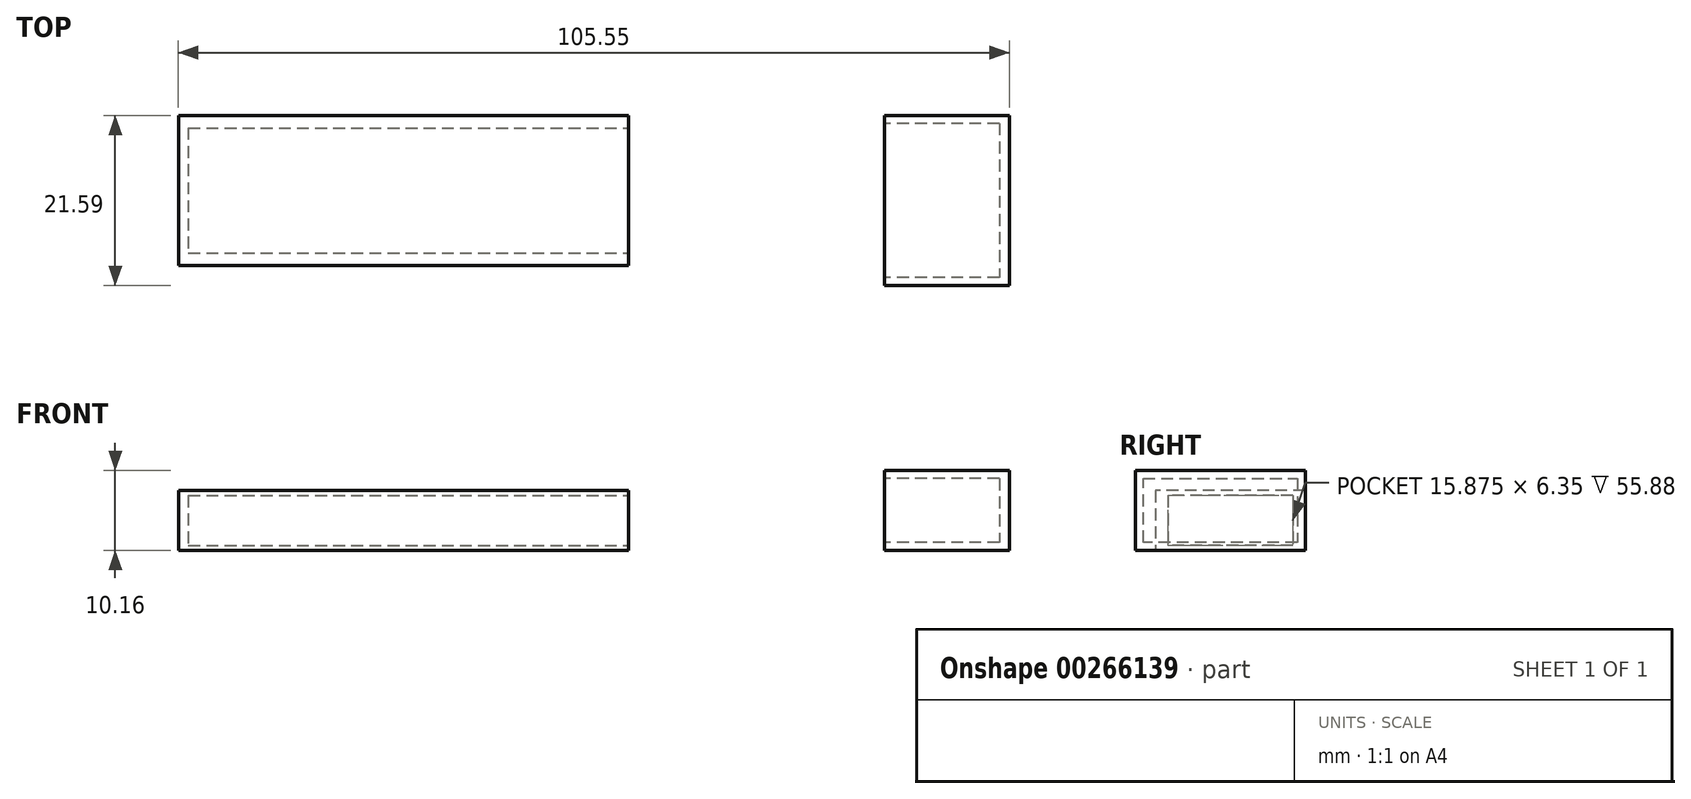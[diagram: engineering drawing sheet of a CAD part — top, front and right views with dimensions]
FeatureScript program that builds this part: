
annotation { "Feature Type Name" : "Feature", "Feature Type Description" : "" }
export const myFeature = defineFeature(function(context is Context, id is Id, definition is map)
    precondition{}
    {
        {
            var Q0;
            Q0=qCreatedBy(makeId("Top.planeOp"),FACE);
            var sketch = newSketch(context, id + "F0", { "sketchPlane" : qUnion([Q0])});
            skLineSegment(sketch, "E0.bottom", {"start": v(-57.67, 16.7) * mm, "end": v(-0.52, 16.7) * mm});
            skLineSegment(sketch, "E0.top", {"start": v(-57.67, -2.35) * mm, "end": v(-0.52, -2.35) * mm});
            skLineSegment(sketch, "E0.left", {"start": v(-57.67, 16.7) * mm, "end": v(-57.67, -2.35) * mm});
            skLineSegment(sketch, "E0.right", {"start": v(-0.52, 16.7) * mm, "end": v(-0.52, -2.35) * mm});
            skLineSegment(sketch, "E1.bottom", {"start": v(32, 16.7) * mm, "end": v(47.88, 16.7) * mm});
            skLineSegment(sketch, "E1.top", {"start": v(32, -4.9) * mm, "end": v(47.88, -4.9) * mm});
            skLineSegment(sketch, "E1.left", {"start": v(32, 16.7) * mm, "end": v(32, -4.9) * mm});
            skLineSegment(sketch, "E1.right", {"start": v(47.88, 16.7) * mm, "end": v(47.88, -4.9) * mm});
            skFitSpline(sketch, "E2", {"points": [v(-57.67, 7.17) * mm, v(-71.95, 19.43) * mm, v(-49.66, 49.56) * mm, v(30.53, 57.4) * mm, v(72.3, 17.31) * mm, v(47.88, 5.9) * mm], "startDerivative": vector(-182.05, 0) * mm, "endDerivative": vector(-254.37, 0) * mm});
            skSolve(sketch);
        }
        {
            var Q0;
            Q0=makeQuery(id+"F0.imprint","IMPRINT",FACE,{"disambiguationData":[TD([[makeQuery(id+"F0.imprint","IMPRINT",EDGE,{"derivedFrom":sQuery(id+"F0.wireOp",EDGE,"E0.bottom")}),-1.0]])]});
            extrude(context, id + "F1", {"entities" : qUnion([Q0]), "depth" : 7.62 * mm});
        }
        {
            var Q0;
            Q0=makeQuery(id+"F0.imprint","IMPRINT",FACE,{"disambiguationData":[TD([[makeQuery(id+"F0.imprint","IMPRINT",EDGE,{"derivedFrom":sQuery(id+"F0.wireOp",EDGE,"E1.bottom")}),-1.0]])]});
            extrude(context, id + "F2", {"entities" : qUnion([Q0]), "depth" : 10.16 * mm});
        }
        {
            var Q0;
            Q0=makeQuery(id+"F1.opExtrude","SWEPT_FACE",FACE,{"disambiguationData":[OSD([sQuery(id+"F0.wireOp",EDGE,"E0.right")])]});
            var sketch = newSketch(context, id + "F3", { "sketchPlane" : qUnion([Q0])});
            skLineSegment(sketch, "E3.0", {"start": v(15.11, 6.99) * mm, "end": v(-0.76, 6.99) * mm});
            skLineSegment(sketch, "E3.1", {"start": v(15.11, 6.99) * mm, "end": v(15.11, 0.64) * mm});
            skLineSegment(sketch, "E3.3", {"start": v(-0.76, 6.99) * mm, "end": v(-0.76, 0.63) * mm});
            skLineSegment(sketch, "E4", {"start": v(15.11, 0.63) * mm, "end": v(-0.76, 0.63) * mm});
            skSolve(sketch);
        }
        {
            var Q0;
            Q0=makeQuery(id+"F2.opExtrude","SWEPT_FACE",FACE,{"disambiguationData":[OSD([sQuery(id+"F0.wireOp",EDGE,"E1.left")])]});
            var sketch = newSketch(context, id + "F4", { "sketchPlane" : qUnion([Q0])});
            skLineSegment(sketch, "E5.0", {"start": v(-15.68, 1.02) * mm, "end": v(3.87, 1.02) * mm});
            skLineSegment(sketch, "E5.1", {"start": v(-15.68, 9.14) * mm, "end": v(-15.68, 1.02) * mm});
            skLineSegment(sketch, "E5.2", {"start": v(3.87, 9.14) * mm, "end": v(-15.68, 9.14) * mm});
            skLineSegment(sketch, "E5.3", {"start": v(3.87, 1.02) * mm, "end": v(3.87, 9.14) * mm});
            skSolve(sketch);
        }
        {
            var Q0;
            Q0=makeQuery(id+"F3.imprint","IMPRINT",FACE,{"disambiguationData":[TD([[makeQuery(id+"F3.imprint","IMPRINT",EDGE,{"derivedFrom":sQuery(id+"F3.wireOp",EDGE,"E3.0")}),1.0]])]});
            extrude(context, id + "F5", {"entities" : qUnion([Q0]), "operationType" : NewBodyOperationType.REMOVE, "oppositeDirection" : true, "depth" : 55.88 * mm});
        }
        {
            var Q0;
            Q0=makeQuery(id+"F4.imprint","IMPRINT",FACE,{"disambiguationData":[TD([[makeQuery(id+"F4.imprint","IMPRINT",EDGE,{"derivedFrom":sQuery(id+"F4.wireOp",EDGE,"E5.0")}),1.0]])]});
            extrude(context, id + "F6", {"entities" : qUnion([Q0]), "operationType" : NewBodyOperationType.REMOVE, "oppositeDirection" : true, "depth" : 14.6 * mm});
        }
    });
